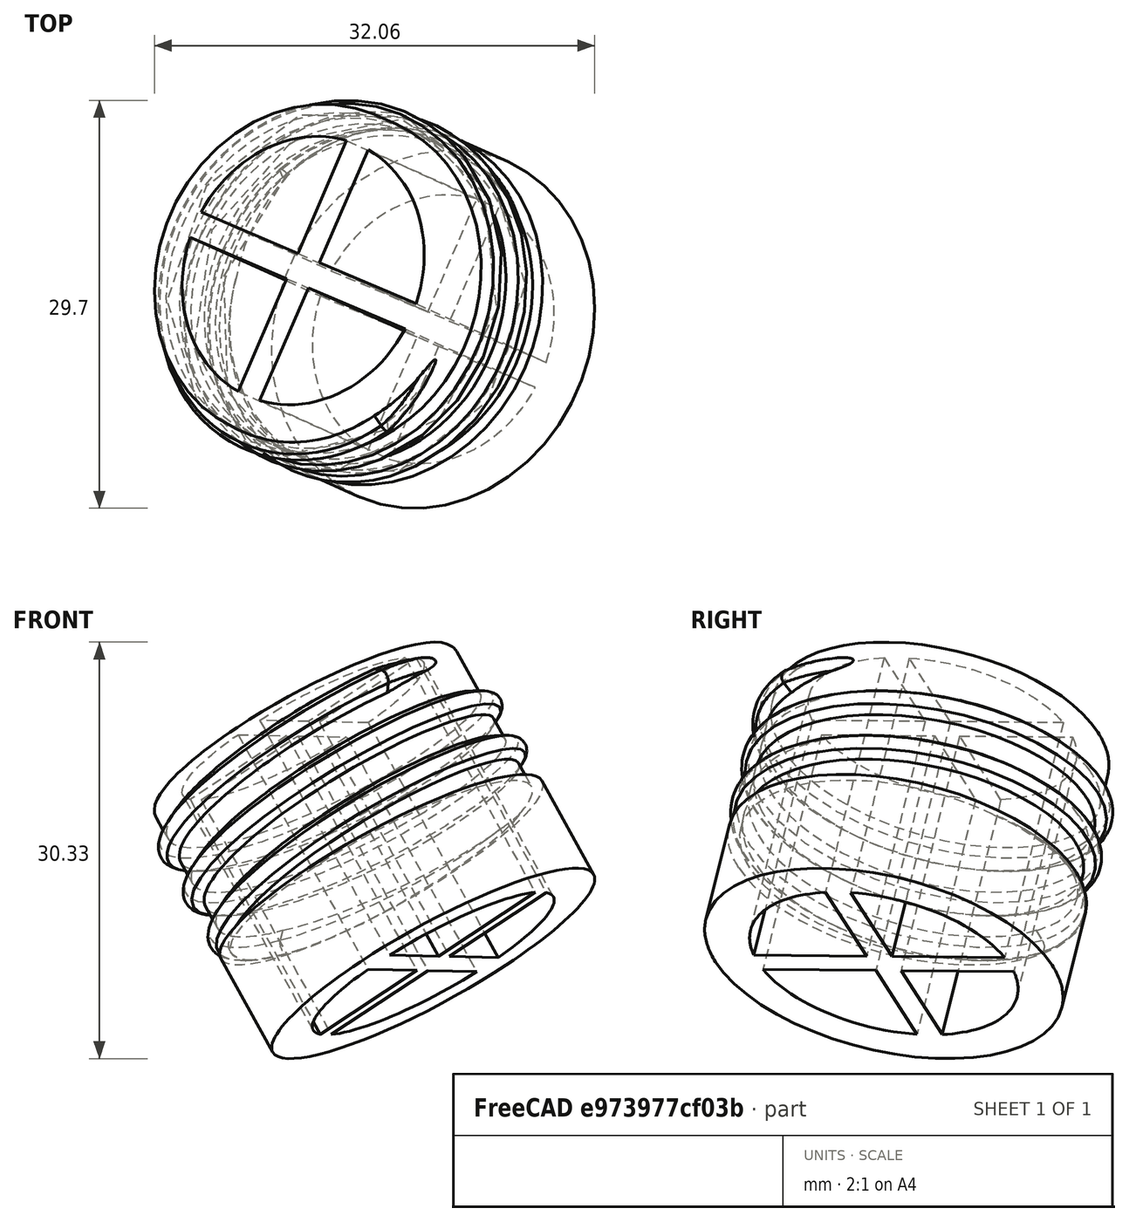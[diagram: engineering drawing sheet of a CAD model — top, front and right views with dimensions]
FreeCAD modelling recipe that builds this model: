
FCSTD DOCUMENT  (FreeCAD 0.14R3700 (Git))
Label: Outils_Goulot_bouteille_FC_rev1
License: CC-BY 3.0
LicenseURL: http://creativecommons.org/licenses/by/3.0/
objects: Part::Feature×1, Sketcher::SketchObject×1, App::MeasureDistance×1
note: 2 computed .brp shape members not serialized (recipe doc carries the construction recipe); baked Part::Feature solids carry a one-line shape summary decoded from their .brp

FEATURE [Part::Feature] Part__Feature  label="FV_082_ASM003"
  Placement = pos=(-8.58915,7.3917,208.67) rot=(-0.495422,0.758319,0.423685;3.69348rad)
  shape: bbox 32.38 x 30.33 x 30.74 mm, 34 faces (baked)
FEATURE [Sketcher::SketchObject] Sketch
  Placement = pos=(-8.58915,7.3917,208.67) rot=(-0.535329,0.812702,-0.230082;2.85176rad)
  Support = -> Part__Feature [Face1]
  sketch-geometry (2):
    g0: Circle CenterX=-20 CenterY=20 CenterZ=0 NormalX=0 NormalY=0 NormalZ=1 Radius=10
    g1: Circle CenterX=0 CenterY=0 CenterZ=0 NormalX=0 NormalY=0 NormalZ=1 Radius=0
  constraints (2):
    c: Coincident(g1,g-1)
    c: Radius(g0) = 10
FEATURE [App::MeasureDistance] Distance001  label="Distance: 26.700"
  Distance = 26.7
  P1 = (-3.288,19.6435,208.551)
  P2 = (-13.8903,-4.86008,208.79)
